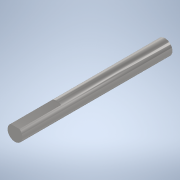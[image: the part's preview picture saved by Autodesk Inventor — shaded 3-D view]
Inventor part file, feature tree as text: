
AUTODESK INVENTOR PART (.ipt)
format: ipt  version: 2022 (Build 260153000, 153)  size: 108,544 bytes
history: native  units: in
note: dims shown in document units (in); Inventor stores cm internally (conversion verified against a paired STEP export)
features: extrude x2, sketch x2
ambient origin geometry x8: Origin, YZ Plane, XZ Plane, XY Plane, X Axis, Y Axis, Z Axis, Center Point
bodies: Solid1 (feature_tree)
feature tree (4):
  extrude  "Extrusion1"  Depth=3.9764in TaperAngle=0.0deg
  extrude  "Extrusion2"  Depth=1.1024in
  sketch  "Sketch1"  dims[d0=0.3937in d1=3.9764in d2=0.0in]
  sketch  "Sketch2"  dims[d3=0.3937in d4=0.1575in d5=1.1024in d6=0.0in]
